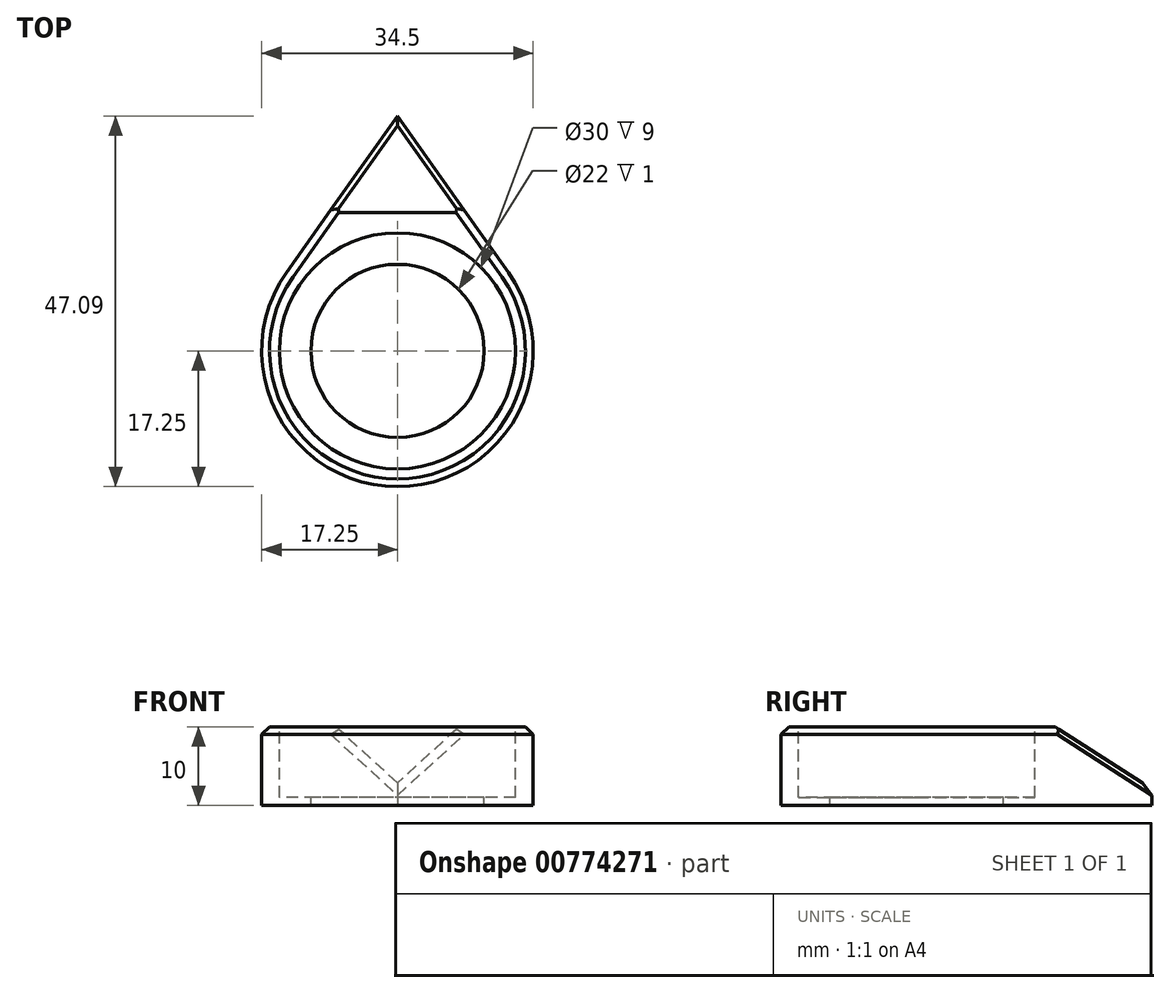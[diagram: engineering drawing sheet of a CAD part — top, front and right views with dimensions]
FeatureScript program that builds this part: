
annotation { "Feature Type Name" : "Feature", "Feature Type Description" : "" }
export const myFeature = defineFeature(function(context is Context, id is Id, definition is map)
    precondition{}
    {
        {
            var Q0;
            Q0=qCreatedBy(makeId("Top.planeOp"),FACE);
            var sketch = newSketch(context, id + "F0", { "sketchPlane" : qUnion([Q0])});
            skCircle(sketch, "E0", {"center": v(0, 0) * mm, "radius": 11 * mm});
            skCircle(sketch, "E1", {"center": v(0, 0) * mm, "radius": 14.75 * mm});
            skSolve(sketch);
        }
        {
            var Q0;
            Q0=makeQuery(id+"F0.imprint","IMPRINT",FACE,{"disambiguationData":[TD([[makeQuery(id+"F0.imprint","IMPRINT",EDGE,{"derivedFrom":sQuery(id+"F0.wireOp",EDGE,"E0")}),-1.0]])]});
            extrude(context, id + "F1", {"entities" : qUnion([Q0]), "depth" : 0.5 * mm, "offsetDistance" : 25 * mm});
        }
        {
            var Q0;
            Q0=qCreatedBy(makeId("Top.planeOp"),FACE);
            var sketch = newSketch(context, id + "F2", { "sketchPlane" : qUnion([Q0])});
            skArc(sketch, "E2.0", {"start": v(-14.08, 9.97) * mm, "mid": v(0, -17.25) * mm, "end": v(14.08, 9.97) * mm});
            skLineSegment(sketch, "E3", {"start": v(-14.08, 9.97) * mm, "end": v(0, 29.84) * mm});
            skLineSegment(sketch, "E4.MirrorCS", {"start": v(14.08, 9.97) * mm, "end": v(0, 29.84) * mm});
            skSolve(sketch);
        }
        {
            var Q0;
            Q0=makeQuery(id+"F2.imprint","IMPRINT",FACE,{"disambiguationData":[TD([[makeQuery(id+"F2.imprint","IMPRINT",EDGE,{"derivedFrom":sQuery(id+"F2.wireOp",EDGE,"E2.0")}),1.0]])]});
            extrude(context, id + "F3", {"entities" : qUnion([Q0]), "operationType" : NewBodyOperationType.ADD, "depth" : 10 * mm, "offsetDistance" : 25 * mm});
        }
        {
            var Q0;
            Q0=makeQuery(id+"F3.opExtrude","CAP_FACE",FACE,{"disambiguationData":[OSD([sQuery(id+"F2.wireOp",EDGE,"E2.0"),sQuery(id+"F2.wireOp",EDGE,"E3"),sQuery(id+"F2.wireOp",EDGE,"E4.MirrorCS")])],"isStart":false});
            var sketch = newSketch(context, id + "F4", { "sketchPlane" : qUnion([Q0])});
            skCircle(sketch, "E5", {"center": v(0, 0) * mm, "radius": 15 * mm});
            skSolve(sketch);
        }
        {
            var Q0;
            Q0=makeQuery(id+"F4.imprint","IMPRINT",FACE,{"disambiguationData":[TD([[makeQuery(id+"F4.imprint","IMPRINT",EDGE,{"derivedFrom":sQuery(id+"F4.wireOp",EDGE,"E5")}),1.0]])]});
            extrude(context, id + "F5", {"entities" : qUnion([Q0]), "operationType" : NewBodyOperationType.REMOVE, "oppositeDirection" : true, "depth" : 9 * mm, "offsetDistance" : 25 * mm});
        }
        {
            var Q0;
            Q0=makeQuery(id+"F5.boolean.opBoolean","COPY",FACE,{"derivedFrom":makeQuery(id+"F5.opExtrude","CAP_FACE",FACE,{"disambiguationData":[OSD([sQuery(id+"F4.wireOp",EDGE,"E5")])],"isStart":false})});
            var sketch = newSketch(context, id + "F6", { "sketchPlane" : qUnion([Q0])});
            skCircle(sketch, "E6", {"center": v(0, 0) * mm, "radius": 11 * mm});
            skSolve(sketch);
        }
        {
            var Q0;
            Q0=qCreatedBy(makeId("Right.planeOp"),FACE);
            var sketch = newSketch(context, id + "F7", { "sketchPlane" : qUnion([Q0])});
            skLineSegment(sketch, "E7", {"start": v(30.53, 10.68) * mm, "end": v(16.53, 10.68) * mm});
            skLineSegment(sketch, "E8", {"start": v(16.53, 10.68) * mm, "end": v(30.52, 1.68) * mm});
            skLineSegment(sketch, "E9", {"start": v(30.52, 1.68) * mm, "end": v(30.53, 10.68) * mm});
            skSolve(sketch);
        }
        {
            var Q0;
            Q0=makeQuery(id+"F7.imprint","IMPRINT",FACE,{"disambiguationData":[TD([[makeQuery(id+"F7.imprint","IMPRINT",EDGE,{"derivedFrom":sQuery(id+"F7.wireOp",EDGE,"E7")}),1.0]])]});
            extrude(context, id + "F8", {"entities" : qUnion([Q0]), "operationType" : NewBodyOperationType.REMOVE, "endBound" : BoundingType.SYMMETRIC, "depth" : 25 * mm, "offsetDistance" : 25 * mm});
        }
        {
            var Q0;
            Q0=makeQuery(id+"F3.opExtrude","CAP_EDGE",EDGE,{"disambiguationData":[OSD([sQuery(id+"F2.wireOp",EDGE,"E4.MirrorCS")])],"isStart":false});
            var Q1;
            Q1=makeQuery(id+"F8.boolean.opBoolean","INTERSECT",EDGE,{"derivedFrom":[makeQuery(id+"F3.opExtrude","SWEPT_FACE",FACE,{"disambiguationData":[OSD([sQuery(id+"F2.wireOp",EDGE,"E4.MirrorCS")])]}),makeQuery(id+"F8.opExtrude","SWEPT_FACE",FACE,{"disambiguationData":[OSD([sQuery(id+"F7.wireOp",EDGE,"E8")])]})]});
            var Q2;
            Q2=makeQuery(id+"F8.boolean.opBoolean","INTERSECT",EDGE,{"derivedFrom":[makeQuery(id+"F3.opExtrude","SWEPT_FACE",FACE,{"disambiguationData":[OSD([sQuery(id+"F2.wireOp",EDGE,"E3")])]}),makeQuery(id+"F8.opExtrude","SWEPT_FACE",FACE,{"disambiguationData":[OSD([sQuery(id+"F7.wireOp",EDGE,"E8")])]})]});
            chamfer(context, id + "F9", {"entities" : qUnion([Q0, Q1, Q2]), "width" : 1 * mm, "tangentPropagation" : true});
        }
        {
            var Q0;
            Q0 = qSketchRegion(id + "F6", true);
            extrude(context, id + "F10", {"entities" : qUnion([Q0]), "operationType" : NewBodyOperationType.REMOVE, "oppositeDirection" : true, "depth" : 25 * mm, "offsetDistance" : 25 * mm});
        }
    });
